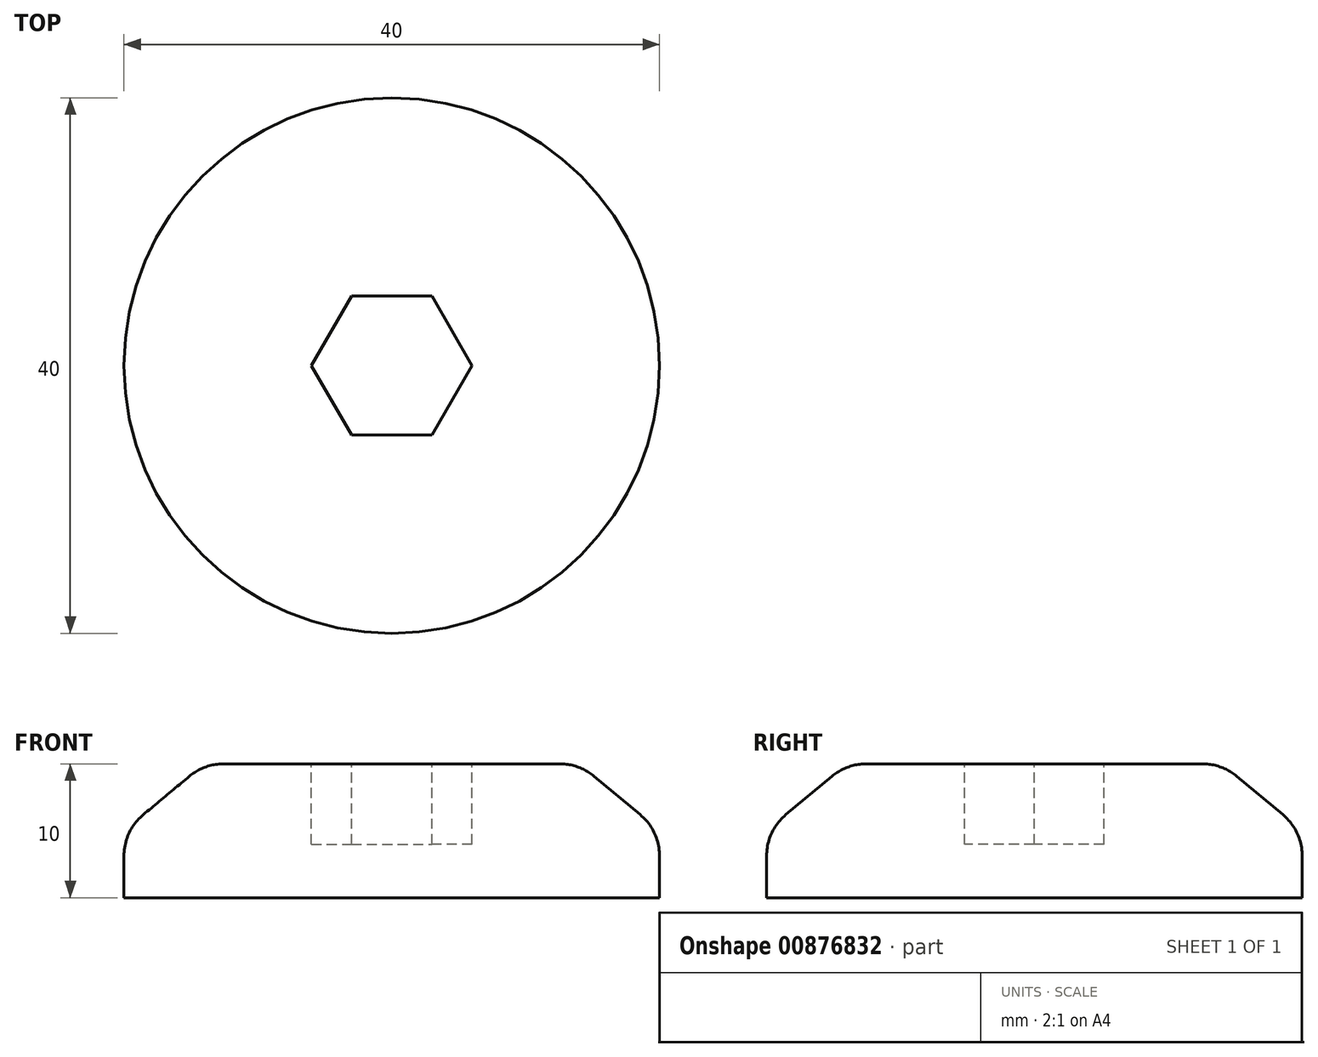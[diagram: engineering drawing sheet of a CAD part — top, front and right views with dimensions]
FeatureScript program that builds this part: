
annotation { "Feature Type Name" : "Feature", "Feature Type Description" : "" }
export const myFeature = defineFeature(function(context is Context, id is Id, definition is map)
    precondition{}
    {
        {
            var Q0;
            Q0=qCreatedBy(makeId("Top.planeOp"),FACE);
            var sketch = newSketch(context, id + "F0", { "sketchPlane" : qUnion([Q0])});
            skCircle(sketch, "E0", {"center": v(0, 0) * mm, "radius": 20 * mm});
            skSolve(sketch);
        }
        {
            var Q0;
            Q0 = qSketchRegion(id + "F0", true);
            extrude(context, id + "F1", {"entities" : qUnion([Q0]), "depth" : 10 * mm, "offsetDistance" : 25 * mm});
        }
        {
            var Q0;
            Q0=makeQuery(id+"F1.opExtrude","CAP_FACE",FACE,{"disambiguationData":[OSD([sQuery(id+"F0.wireOp",EDGE,"E0")])],"isStart":false});
            var sketch = newSketch(context, id + "F2", { "sketchPlane" : qUnion([Q0])});
            skCircle(sketch, "E1.cCircle", {"center": v(0, 0) * mm, "radius": 6 * mm, "construction": true});
            skLineSegment(sketch, "E1.0", {"start": v(6, 0) * mm, "end": v(3, -5.2) * mm});
            skLineSegment(sketch, "E1.1", {"start": v(3, -5.2) * mm, "end": v(-3, -5.2) * mm});
            skLineSegment(sketch, "E1.2", {"start": v(-3, -5.2) * mm, "end": v(-6, 0) * mm});
            skLineSegment(sketch, "E1.3", {"start": v(-6, 0) * mm, "end": v(-3, 5.2) * mm});
            skLineSegment(sketch, "E1.4", {"start": v(-3, 5.2) * mm, "end": v(3, 5.2) * mm});
            skLineSegment(sketch, "E1.5", {"start": v(3, 5.2) * mm, "end": v(6, 0) * mm});
            skSolve(sketch);
        }
        {
            var Q0;
            Q0=makeQuery(id+"F2.imprint","IMPRINT",FACE,{"disambiguationData":[TD([[makeQuery(id+"F2.imprint","IMPRINT",EDGE,{"derivedFrom":sQuery(id+"F2.wireOp",EDGE,"E1.0")}),-1.0]])]});
            extrude(context, id + "F3", {"entities" : qUnion([Q0]), "operationType" : NewBodyOperationType.REMOVE, "oppositeDirection" : true, "depth" : 6 * mm, "offsetDistance" : 25 * mm});
        }
        {
            var Q0;
            Q0=makeQuery(id+"F1.opExtrude","CAP_EDGE",EDGE,{"disambiguationData":[OSD([sQuery(id+"F0.wireOp",EDGE,"E0")])],"isStart":false});
            chamfer(context, id + "F4", {"entities" : qUnion([Q0]), "chamferType" : ChamferType.TWO_OFFSETS, "width1" : 6 * mm, "oppositeDirection" : false, "width2" : 5 * mm, "tangentPropagation" : true});
        }
        {
            var Q0;
            {var subQ0=sQuery(id+"F0.wireOp",EDGE,"E0");Q0=makeQuery(id+"F4.opChamfer","BLEND_EDGE",EDGE,{"blendedFrom":[makeQuery(id+"F1.opExtrude","CAP_EDGE",EDGE,{"disambiguationData":[OSD([subQ0])],"isStart":false}),makeQuery(id+"F1.opExtrude","CAP_FACE",FACE,{"disambiguationData":[OSD([subQ0])],"isStart":false})],"blendedInto":[makeQuery(id+"F1.opExtrude","CAP_FACE",FACE,{"disambiguationData":[OSD([subQ0])],"isStart":false})]});}
            var Q1;
            {var subQ0=sQuery(id+"F0.wireOp",EDGE,"E0");Q1=makeQuery(id+"F4.opChamfer","BLEND_EDGE",EDGE,{"blendedFrom":[makeQuery(id+"F1.opExtrude","CAP_EDGE",EDGE,{"disambiguationData":[OSD([subQ0])],"isStart":false}),makeQuery(id+"F1.opExtrude","SWEPT_FACE",FACE,{"disambiguationData":[OSD([subQ0])]})],"blendedInto":[makeQuery(id+"F1.opExtrude","SWEPT_FACE",FACE,{"disambiguationData":[OSD([subQ0])]})]});}
            fillet(context, id + "F5", {"entities" : qUnion([Q0, Q1]), "radius" : 4 * mm, "tangentPropagation" : true, "allowEdgeOverflow" : false});
        }
    });
